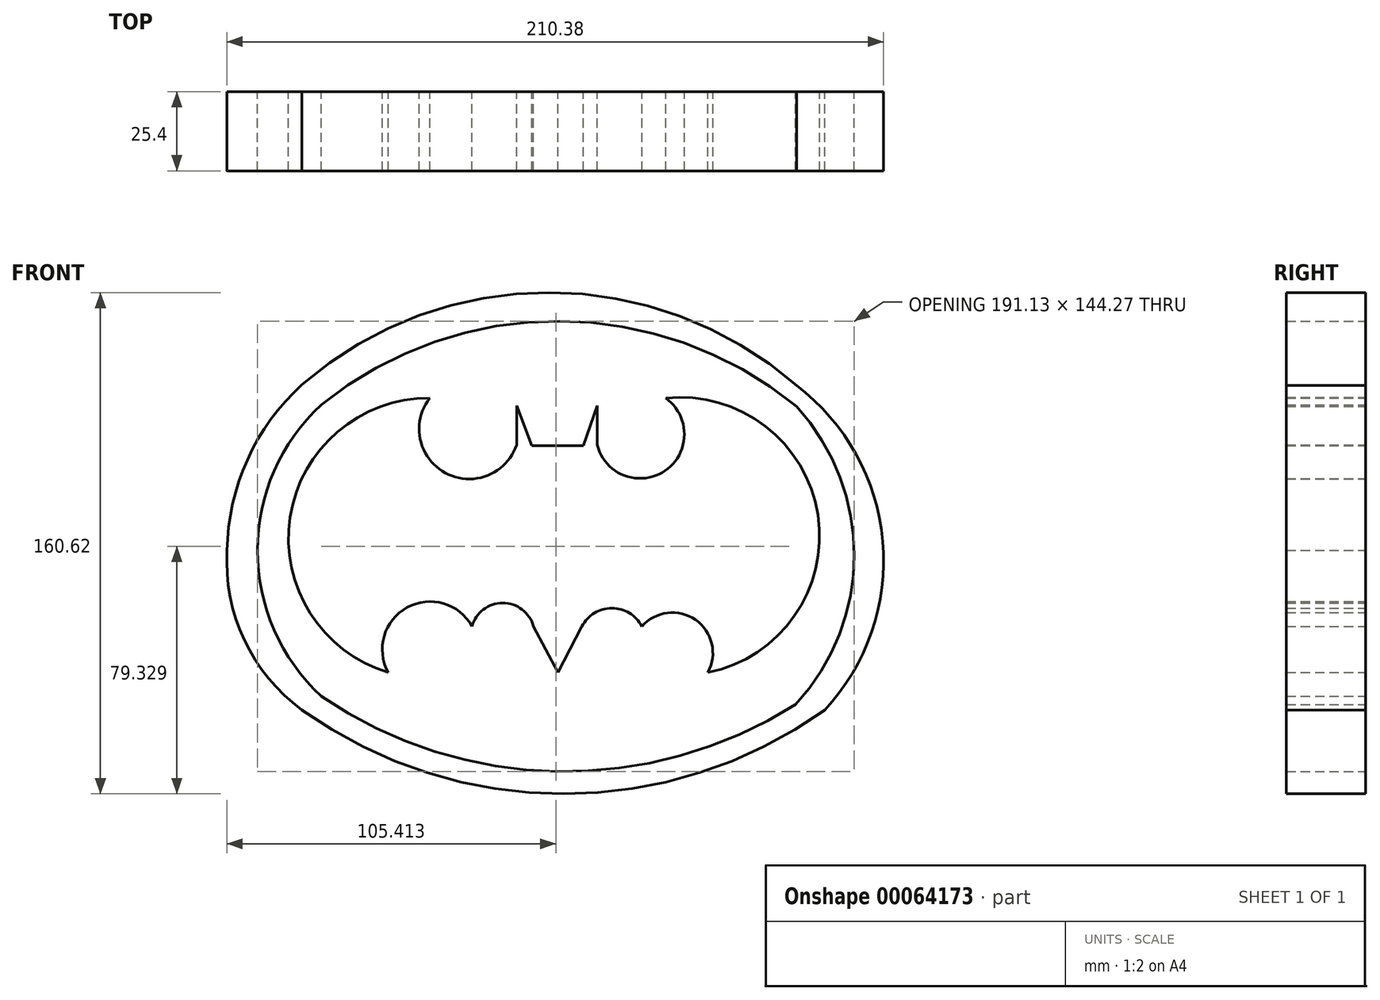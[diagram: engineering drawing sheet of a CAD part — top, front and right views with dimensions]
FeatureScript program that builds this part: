
annotation { "Feature Type Name" : "Feature", "Feature Type Description" : "" }
export const myFeature = defineFeature(function(context is Context, id is Id, definition is map)
    precondition{}
    {
        {
            var Q0;
            Q0=qCreatedBy(makeId("Front.planeOp"),FACE);
            var sketch = newSketch(context, id + "F0", { "sketchPlane" : qUnion([Q0])});
            skLineSegment(sketch, "E0", {"start": v(-8.37, 47.02) * mm, "end": v(8.12, 47.02) * mm});
            skLineSegment(sketch, "E1", {"start": v(-8.37, 47.02) * mm, "end": v(-13.3, 59.82) * mm});
            skLineSegment(sketch, "E2", {"start": v(8.12, 47.02) * mm, "end": v(12.56, 59.82) * mm});
            skLineSegment(sketch, "E3", {"start": v(-13.3, 59.82) * mm, "end": v(-13.3, 47.27) * mm});
            skLineSegment(sketch, "E4", {"start": v(12.56, 59.82) * mm, "end": v(12.56, 47.27) * mm});
            skArc(sketch, "E5", {"start": v(-41.11, 62.28) * mm, "mid": v(-36.09, 38.31) * mm, "end": v(-13.3, 47.27) * mm});
            skArc(sketch, "E6", {"start": v(12.56, 47.27) * mm, "mid": v(34.3, 39.05) * mm, "end": v(34.47, 62.28) * mm});
            skArc(sketch, "E7", {"start": v(-41.11, 62.28) * mm, "mid": v(-85.85, 24.1) * mm, "end": v(-54.4, -25.6) * mm});
            skArc(sketch, "E8", {"start": v(48, -25.6) * mm, "mid": v(83.22, 24.8) * mm, "end": v(34.47, 62.28) * mm});
            skArc(sketch, "E9", {"start": v(-27.57, -10.83) * mm, "mid": v(-48.38, -4.8) * mm, "end": v(-54.4, -25.6) * mm});
            skArc(sketch, "E10", {"start": v(-7.88, -10.83) * mm, "mid": v(-17.73, -3.34) * mm, "end": v(-27.57, -10.83) * mm});
            skLineSegment(sketch, "E11", {"start": v(-7.88, -10.83) * mm, "end": v(0, -25.6) * mm});
            skLineSegment(sketch, "E12", {"start": v(0, -25.6) * mm, "end": v(7.63, -10.83) * mm});
            skArc(sketch, "E13", {"start": v(26.83, -10.83) * mm, "mid": v(17.23, -4.99) * mm, "end": v(7.63, -10.83) * mm});
            skArc(sketch, "E14", {"start": v(48, -25.6) * mm, "mid": v(44.02, -8.76) * mm, "end": v(26.83, -10.83) * mm});
            skArc(sketch, "E15", {"start": v(-75.87, 60.18) * mm, "mid": v(-96.3, 13.48) * mm, "end": v(-75.87, -33.21) * mm});
            skArc(sketch, "E16", {"start": v(76.07, -35.85) * mm, "mid": v(94.84, 11.82) * mm, "end": v(76.37, 59.6) * mm});
            skArc(sketch, "E17", {"start": v(76.37, 59.6) * mm, "mid": v(0.35, 86.96) * mm, "end": v(-75.87, 60.18) * mm});
            skArc(sketch, "E18", {"start": v(-75.87, -33.21) * mm, "mid": v(-0.3, -57.3) * mm, "end": v(76.07, -35.85) * mm});
            skArc(sketch, "E19", {"start": v(-82.02, 66.62) * mm, "mid": v(-99.53, 42.54) * mm, "end": v(-106.03, 13.48) * mm});
            skPoint(sketch, "E19.endSnap0", {"position": v(-96.3, 13.48) * mm});
            skArc(sketch, "E20", {"start": v(-106.03, 13.48) * mm, "mid": v(-100.55, -15.13) * mm, "end": v(-82.02, -37.6) * mm});
            skArc(sketch, "E21", {"start": v(-82.02, -37.6) * mm, "mid": v(1.71, -64.5) * mm, "end": v(85.44, -37.6) * mm});
            skArc(sketch, "E22", {"start": v(85.44, -37.6) * mm, "mid": v(103.97, 16.38) * mm, "end": v(76.37, 66.33) * mm});
            skArc(sketch, "E23", {"start": v(76.37, 66.33) * mm, "mid": v(-2.77, 96.12) * mm, "end": v(-82.02, 66.62) * mm});
            skSolve(sketch);
        }
        {
            var Q0;
            Q0=makeQuery(id+"F0.imprint","IMPRINT",FACE,{"disambiguationData":[TD([[makeQuery(id+"F0.imprint","IMPRINT",EDGE,{"derivedFrom":sQuery(id+"F0.wireOp",EDGE,"E15")}),-1.0]])]});
            var Q1;
            Q1=makeQuery(id+"F0.imprint","IMPRINT",FACE,{"disambiguationData":[TD([[makeQuery(id+"F0.imprint","IMPRINT",EDGE,{"derivedFrom":sQuery(id+"F0.wireOp",EDGE,"E0")}),-1.0]])]});
            extrude(context, id + "F1", {"entities" : qUnion([Q0, Q1]), "depth" : 25.4 * mm});
        }
    });
